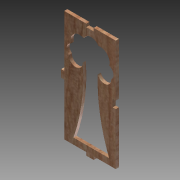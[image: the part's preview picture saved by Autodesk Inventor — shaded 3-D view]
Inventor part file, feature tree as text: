
AUTODESK INVENTOR PART (.ipt)
format: ipt  version: 2015 (Build 190159000, 159)  size: 179,200 bytes
history: native  units: in
note: dims shown in document units (in); Inventor stores cm internally (conversion verified against a paired STEP export)
features: extrude x4, sketch x4
ambient origin geometry x8: Origin, YZ Plane, XZ Plane, XY Plane, X Axis, Y Axis, Z Axis, Center Point
bodies: Solid1 (feature_tree)
feature tree (8):
  extrude  "Extrusion1"  Depth=2.084in
  sketch  "Sketch2"  dims[d2=0.125in d3=0.0in d4=0.15in]
  extrude  "Extrusion2"  Depth=0.125in
  extrude  "Extrusion3"  Depth=0.125in
  sketch  "Sketch3"  dims[d5=0.3in d6=0.125in]
  extrude  "Extrusion4"  Depth=0.3in
  sketch  "Sketch1"  dims[d0=4.5in d1=2.084in]
  sketch  "Sketch4"  dims[d7=0.15in d8=0.3in d9=0.125in d13=0.3in d14=0.15in d15=0.125in d16=0.125in d17=0.0in d18=0.125in d19=0.0in d20=0.3in d21=0.15in d22=0.125in d23=2.8125in d24=0.25in d25=7.0in d26=0.25in d28=7.0in d29=1.041in d30=2.8125in d31=1.0in d32=0.0in]
